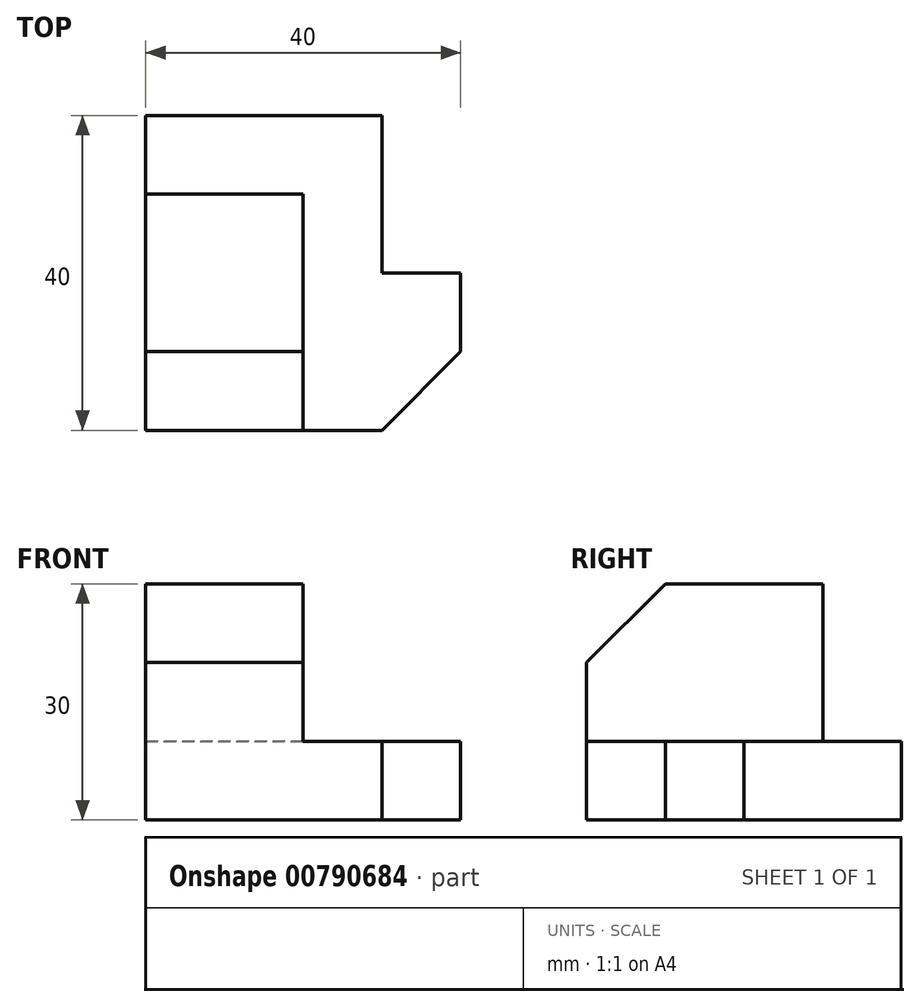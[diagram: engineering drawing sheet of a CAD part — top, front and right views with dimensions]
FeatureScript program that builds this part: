
annotation { "Feature Type Name" : "Feature", "Feature Type Description" : "" }
export const myFeature = defineFeature(function(context is Context, id is Id, definition is map)
    precondition{}
    {
        {
            var Q0;
            Q0=qCreatedBy(makeId("Front.planeOp"),FACE);
            var sketch = newSketch(context, id + "F0", { "sketchPlane" : qUnion([Q0])});
            skLineSegment(sketch, "E0", {"start": v(0, 0) * mm, "end": v(0, 40) * mm});
            skLineSegment(sketch, "E1", {"start": v(0, 40) * mm, "end": v(40, 40) * mm});
            skLineSegment(sketch, "E2", {"start": v(40, 40) * mm, "end": v(40, 0) * mm});
            skLineSegment(sketch, "E3", {"start": v(40, 0) * mm, "end": v(0, 0) * mm});
            skSolve(sketch);
        }
        {
            var Q0;
            Q0 = qSketchRegion(id + "F0", true);
            extrude(context, id + "F1", {"entities" : qUnion([Q0]), "depth" : 40 * mm, "offsetDistance" : 25 * mm});
        }
        {
            var Q0;
            Q0=makeQuery(id+"F1.opExtrude","SWEPT_FACE",FACE,{"disambiguationData":[OSD([sQuery(id+"F0.wireOp",EDGE,"E1")])]});
            var sketch = newSketch(context, id + "F2", { "sketchPlane" : qUnion([Q0])});
            skLineSegment(sketch, "E4", {"start": v(30, 0) * mm, "end": v(30, -20) * mm});
            skLineSegment(sketch, "E5", {"start": v(30, -20) * mm, "end": v(40, -20) * mm});
            skLineSegment(sketch, "E6", {"start": v(40, -20) * mm, "end": v(40, 0) * mm});
            skLineSegment(sketch, "E7", {"start": v(40, 0) * mm, "end": v(30, 0) * mm});
            skSolve(sketch);
        }
        {
            var Q0;
            Q0 = qSketchRegion(id + "F2", true);
            extrude(context, id + "F3", {"entities" : qUnion([Q0]), "operationType" : NewBodyOperationType.REMOVE, "endBound" : BoundingType.THROUGH_ALL, "oppositeDirection" : true, "depth" : 25 * mm, "offsetDistance" : 25 * mm});
        }
        {
            var Q0;
            Q0=makeQuery(id+"F1.opExtrude","SWEPT_FACE",FACE,{"disambiguationData":[OSD([sQuery(id+"F0.wireOp",EDGE,"E1")])]});
            var sketch = newSketch(context, id + "F4", { "sketchPlane" : qUnion([Q0])});
            skLineSegment(sketch, "E8", {"start": v(30, -40) * mm, "end": v(40, -40) * mm});
            skLineSegment(sketch, "E9", {"start": v(40, -40) * mm, "end": v(40, -30) * mm});
            skLineSegment(sketch, "E10", {"start": v(40, -30) * mm, "end": v(30, -40) * mm});
            skSolve(sketch);
        }
        {
            var Q0;
            Q0 = qSketchRegion(id + "F4", true);
            extrude(context, id + "F5", {"entities" : qUnion([Q0]), "operationType" : NewBodyOperationType.REMOVE, "endBound" : BoundingType.THROUGH_ALL, "oppositeDirection" : true, "depth" : 25 * mm, "offsetDistance" : 25 * mm});
        }
        {
            var Q0;
            Q0=makeQuery(id+"F1.opExtrude","SWEPT_FACE",FACE,{"disambiguationData":[OSD([sQuery(id+"F0.wireOp",EDGE,"E1")])]});
            var sketch = newSketch(context, id + "F6", { "sketchPlane" : qUnion([Q0])});
            skLineSegment(sketch, "E11", {"start": v(0, 0) * mm, "end": v(30, 0) * mm});
            skLineSegment(sketch, "E12", {"start": v(30, 0) * mm, "end": v(30, -20) * mm});
            skLineSegment(sketch, "E13", {"start": v(30, -20) * mm, "end": v(40, -20) * mm});
            skLineSegment(sketch, "E14", {"start": v(40, -20) * mm, "end": v(40, -30) * mm});
            skLineSegment(sketch, "E15", {"start": v(40, -30) * mm, "end": v(30, -40) * mm});
            skLineSegment(sketch, "E16", {"start": v(30, -40) * mm, "end": v(20, -40) * mm});
            skLineSegment(sketch, "E17", {"start": v(20, -40) * mm, "end": v(20, -10) * mm});
            skLineSegment(sketch, "E18", {"start": v(20, -10) * mm, "end": v(0, -10) * mm});
            skLineSegment(sketch, "E19", {"start": v(0, -10) * mm, "end": v(0, 0) * mm});
            skSolve(sketch);
        }
        {
            var Q0;
            Q0 = qSketchRegion(id + "F6", true);
            extrude(context, id + "F7", {"entities" : qUnion([Q0]), "operationType" : NewBodyOperationType.REMOVE, "oppositeDirection" : true, "depth" : 20 * mm, "offsetDistance" : 25 * mm});
        }
        {
            var Q0;
            Q0=makeQuery(id+"F1.opExtrude","SWEPT_FACE",FACE,{"disambiguationData":[OSD([sQuery(id+"F0.wireOp",EDGE,"E1")])]});
            var sketch = newSketch(context, id + "F8", { "sketchPlane" : qUnion([Q0])});
            skLineSegment(sketch, "E20", {"start": v(20, -40) * mm, "end": v(20, -10) * mm});
            skLineSegment(sketch, "E21", {"start": v(20, -10) * mm, "end": v(0, -10) * mm});
            skLineSegment(sketch, "E22", {"start": v(0, -10) * mm, "end": v(0, -40) * mm});
            skLineSegment(sketch, "E23", {"start": v(0, -40) * mm, "end": v(20, -40) * mm});
            skSolve(sketch);
        }
        {
            var Q0;
            Q0 = qSketchRegion(id + "F8", true);
            extrude(context, id + "F9", {"entities" : qUnion([Q0]), "operationType" : NewBodyOperationType.REMOVE, "oppositeDirection" : true, "depth" : 10 * mm, "offsetDistance" : 25 * mm});
        }
        {
            var Q0;
            Q0=makeQuery(id+"F7.boolean.opBoolean","COPY",FACE,{"derivedFrom":makeQuery(id+"F7.opExtrude","CAP_FACE",FACE,{"disambiguationData":[OSD([sQuery(id+"F6.wireOp",EDGE,"E11"),sQuery(id+"F6.wireOp",EDGE,"E12"),sQuery(id+"F6.wireOp",EDGE,"E13"),sQuery(id+"F6.wireOp",EDGE,"E14"),sQuery(id+"F6.wireOp",EDGE,"E15"),sQuery(id+"F6.wireOp",EDGE,"E16"),sQuery(id+"F6.wireOp",EDGE,"E17"),sQuery(id+"F6.wireOp",EDGE,"E18"),sQuery(id+"F6.wireOp",EDGE,"E19")])],"isStart":false})});
            var sketch = newSketch(context, id + "F10", { "sketchPlane" : qUnion([Q0])});
            skLineSegment(sketch, "E24", {"start": v(0, 0) * mm, "end": v(30, 0) * mm});
            skLineSegment(sketch, "E25", {"start": v(30, 0) * mm, "end": v(30, -20) * mm});
            skLineSegment(sketch, "E26", {"start": v(30, -20) * mm, "end": v(40, -20) * mm});
            skLineSegment(sketch, "E27", {"start": v(40, -20) * mm, "end": v(40, -30) * mm});
            skLineSegment(sketch, "E28", {"start": v(40, -30) * mm, "end": v(30, -40) * mm});
            skLineSegment(sketch, "E29", {"start": v(30, -40) * mm, "end": v(20, -40) * mm});
            skLineSegment(sketch, "E30", {"start": v(20, -40) * mm, "end": v(20, -10) * mm});
            skLineSegment(sketch, "E31", {"start": v(20, -10) * mm, "end": v(0, -10) * mm});
            skLineSegment(sketch, "E32", {"start": v(0, -10) * mm, "end": v(0, 0) * mm});
            skSolve(sketch);
        }
        {
            var Q0;
            Q0 = qSketchRegion(id + "F10", true);
            extrude(context, id + "F11", {"entities" : qUnion([Q0]), "operationType" : NewBodyOperationType.REMOVE, "oppositeDirection" : true, "depth" : 10 * mm, "offsetDistance" : 25 * mm});
        }
        {
            var Q0;
            Q0=makeQuery(id+"F11.boolean.opBoolean","MERGE",FACE,{"derivedFrom":[makeQuery(id+"F7.boolean.opBoolean","COPY",FACE,{"derivedFrom":makeQuery(id+"F7.opExtrude","SWEPT_FACE",FACE,{"disambiguationData":[OSD([sQuery(id+"F6.wireOp",EDGE,"E17")])]})}),makeQuery(id+"F11.opExtrude","SWEPT_FACE",FACE,{"disambiguationData":[OSD([sQuery(id+"F10.wireOp",EDGE,"E30")])]})]});
            var sketch = newSketch(context, id + "F12", { "sketchPlane" : qUnion([Q0])});
            skLineSegment(sketch, "E33", {"start": v(-40, 30) * mm, "end": v(-30, 30) * mm});
            skLineSegment(sketch, "E34", {"start": v(-30, 30) * mm, "end": v(-40, 20) * mm});
            skLineSegment(sketch, "E35", {"start": v(-40, 20) * mm, "end": v(-40, 30) * mm});
            skSolve(sketch);
        }
        {
            var Q0;
            Q0 = qSketchRegion(id + "F12", true);
            extrude(context, id + "F13", {"entities" : qUnion([Q0]), "operationType" : NewBodyOperationType.REMOVE, "endBound" : BoundingType.THROUGH_ALL, "oppositeDirection" : true, "depth" : 25 * mm, "offsetDistance" : 25 * mm});
        }
    });
